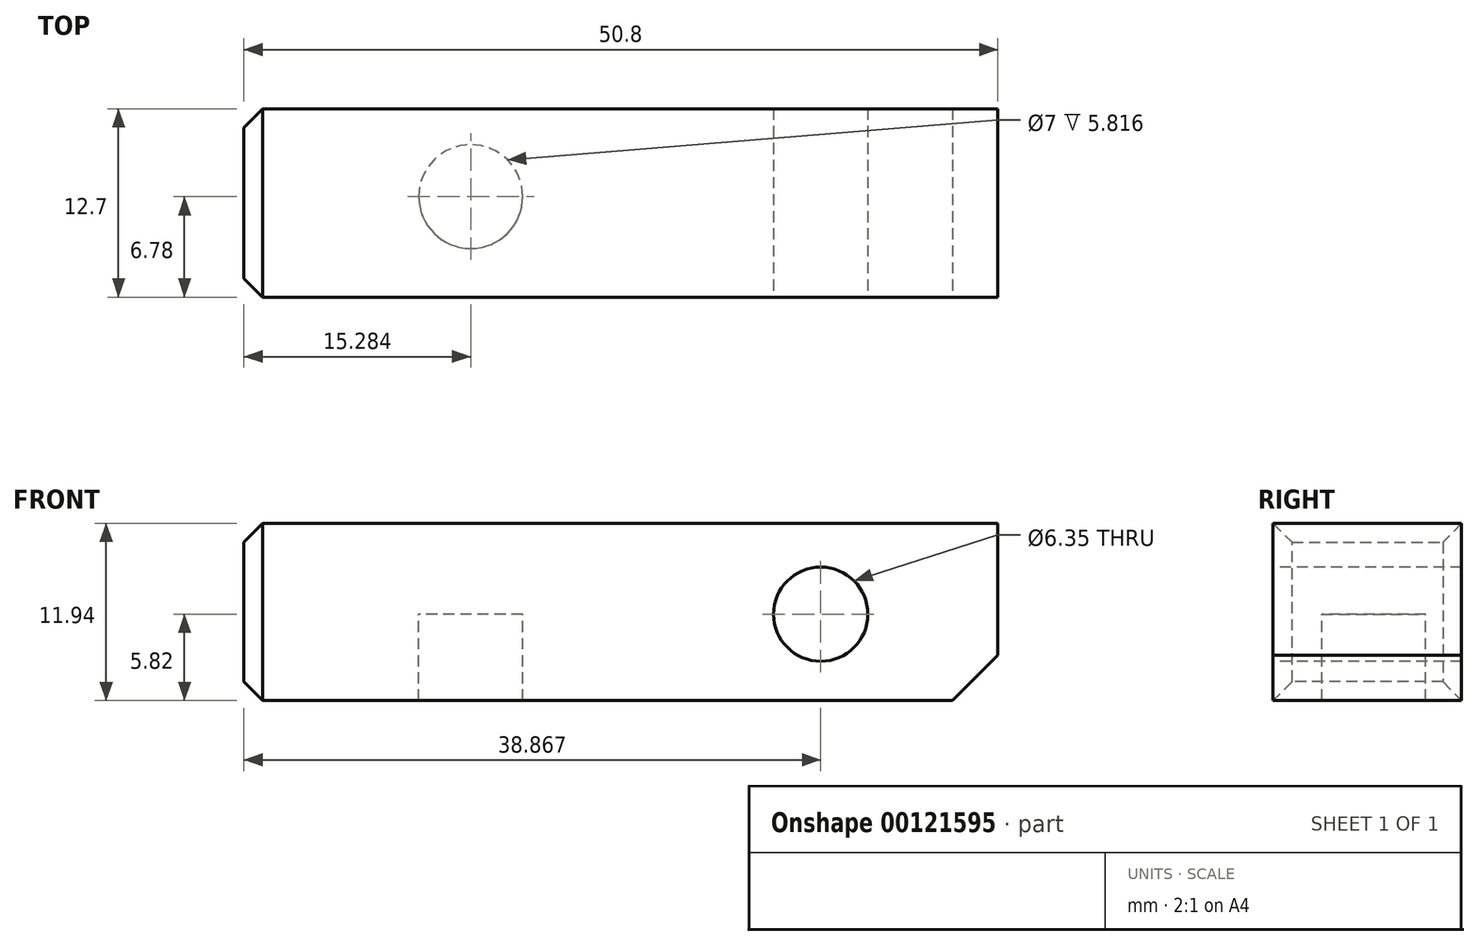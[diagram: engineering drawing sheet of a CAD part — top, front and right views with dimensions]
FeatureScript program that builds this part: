
annotation { "Feature Type Name" : "Feature", "Feature Type Description" : "" }
export const myFeature = defineFeature(function(context is Context, id is Id, definition is map)
    precondition{}
    {
        {
            var Q0;
            Q0=qCreatedBy(makeId("Front.planeOp"),FACE);
            var sketch = newSketch(context, id + "F0", { "sketchPlane" : qUnion([Q0])});
            skLineSegment(sketch, "E0", {"start": v(-30.45, 6.12) * mm, "end": v(20.35, 6.12) * mm});
            skLineSegment(sketch, "E1", {"start": v(20.35, 6.12) * mm, "end": v(20.35, -5.82) * mm});
            skLineSegment(sketch, "E2", {"start": v(20.35, -5.82) * mm, "end": v(-30.45, -5.82) * mm});
            skLineSegment(sketch, "E3", {"start": v(-30.45, -5.82) * mm, "end": v(-30.45, 6.12) * mm});
            skSolve(sketch);
        }
        {
            var Q0;
            Q0 = qSketchRegion(id + "F0", true);
            extrude(context, id + "F1", {"entities" : qUnion([Q0]), "depth" : 12.7 * mm});
        }
        {
            var Q0;
            Q0=makeQuery(id+"F1.opExtrude","CAP_FACE",FACE,{"disambiguationData":[OSD([sQuery(id+"F0.wireOp",EDGE,"E0"),sQuery(id+"F0.wireOp",EDGE,"E1"),sQuery(id+"F0.wireOp",EDGE,"E2"),sQuery(id+"F0.wireOp",EDGE,"E3")])],"isStart":false});
            var sketch = newSketch(context, id + "F2", { "sketchPlane" : qUnion([Q0])});
            skCircle(sketch, "E4", {"center": v(8.42, 0) * mm, "radius": 3.18 * mm});
            skPoint(sketch, "E5.orphan", {"position": v(-30.45, 0.15) * mm});
            skSolve(sketch);
        }
        {
            var Q0;
            Q0=makeQuery(id+"F2.imprint","IMPRINT",FACE,{"disambiguationData":[TD([[makeQuery(id+"F2.imprint","IMPRINT",EDGE,{"derivedFrom":sQuery(id+"F2.wireOp",EDGE,"E4")}),1.0]])]});
            extrude(context, id + "F3", {"entities" : qUnion([Q0]), "operationType" : NewBodyOperationType.REMOVE, "endBound" : BoundingType.THROUGH_ALL, "oppositeDirection" : true, "depth" : 25.4 * mm});
        }
        {
            var Q0;
            Q0=qCreatedBy(makeId("Top.planeOp"),FACE);
            var sketch = newSketch(context, id + "F4", { "sketchPlane" : qUnion([Q0])});
            skLineSegment(sketch, "E6", {"start": v(-18.66, -5.92) * mm, "end": v(-15.17, -5.92) * mm});
            skPoint(sketch, "E7.start.orphan", {"position": v(-32.49, -5.92) * mm});
            skCircle(sketch, "E8", {"center": v(-15.17, -5.92) * mm, "radius": 3.5 * mm});
            skPoint(sketch, "E9.orphan", {"position": v(-30.4, -5.92) * mm});
            skSolve(sketch);
        }
        {
            var Q0;
            Q0 = qSketchRegion(id + "F4", true);
            extrude(context, id + "F5", {"entities" : qUnion([Q0]), "operationType" : NewBodyOperationType.REMOVE, "oppositeDirection" : true, "depth" : 6.35 * mm});
        }
        {
            var Q0;
            Q0=makeQuery(id+"F1.opExtrude","SWEPT_EDGE",EDGE,{"disambiguationData":[OSD([sQuery(id+"F0.wireOp",EDGE,"E1"),sQuery(id+"F0.wireOp",EDGE,"E2")])]});
            chamfer(context, id + "F6", {"entities" : qUnion([Q0]), "width" : 3.05 * mm, "tangentPropagation" : true});
        }
        {
            var Q0;
            Q0=makeQuery(id+"F1.opExtrude","SWEPT_EDGE",EDGE,{"disambiguationData":[OSD([sQuery(id+"F0.wireOp",EDGE,"E0"),sQuery(id+"F0.wireOp",EDGE,"E3")])]});
            var Q1;
            Q1=makeQuery(id+"F1.opExtrude","CAP_EDGE",EDGE,{"disambiguationData":[OSD([sQuery(id+"F0.wireOp",EDGE,"E3")])],"isStart":false});
            var Q2;
            Q2=makeQuery(id+"F1.opExtrude","SWEPT_EDGE",EDGE,{"disambiguationData":[OSD([sQuery(id+"F0.wireOp",EDGE,"E2"),sQuery(id+"F0.wireOp",EDGE,"E3")])]});
            var Q3;
            Q3=makeQuery(id+"F1.opExtrude","CAP_EDGE",EDGE,{"disambiguationData":[OSD([sQuery(id+"F0.wireOp",EDGE,"E3")])],"isStart":true});
            chamfer(context, id + "F7", {"entities" : qUnion([Q0, Q1, Q2, Q3]), "width" : 1.27 * mm, "tangentPropagation" : true});
        }
    });
